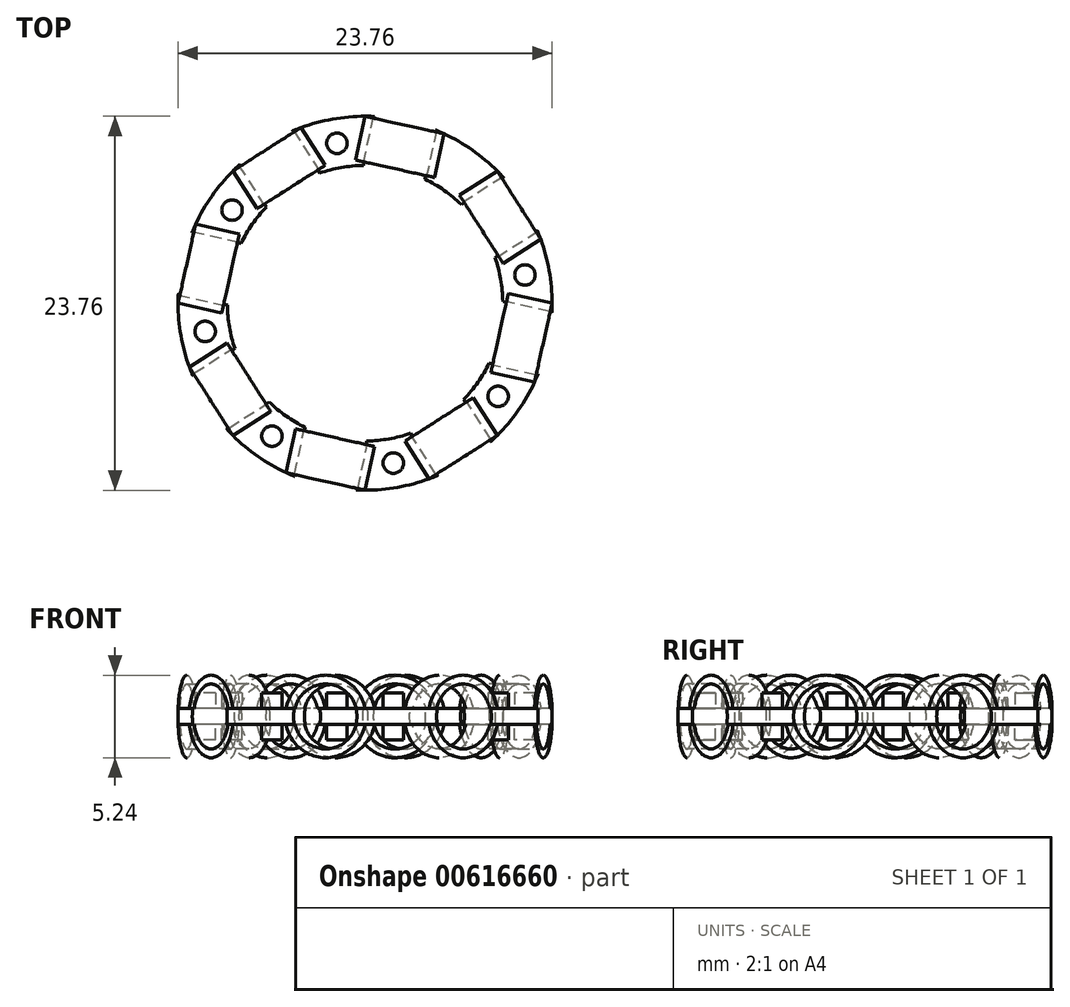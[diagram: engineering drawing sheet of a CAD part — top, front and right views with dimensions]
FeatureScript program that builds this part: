
annotation { "Feature Type Name" : "Feature", "Feature Type Description" : "" }
export const myFeature = defineFeature(function(context is Context, id is Id, definition is map)
    precondition{}
    {
        {
            var Q0;
            Q0=qCreatedBy(makeId("Top.planeOp"),FACE);
            var sketch = newSketch(context, id + "F0", { "sketchPlane" : qUnion([Q0])});
            skCircle(sketch, "E0", {"center": v(0, 0) * mm, "radius": 8.75 * mm});
            skCircle(sketch, "E1", {"center": v(0, 0) * mm, "radius": 11.88 * mm});
            skSolve(sketch);
        }
        {
            var Q0;
            Q0=makeQuery(id+"F0.imprint","IMPRINT",FACE,{"disambiguationData":[TD([[makeQuery(id+"F0.imprint","IMPRINT",EDGE,{"derivedFrom":sQuery(id+"F0.wireOp",EDGE,"E0")}),-1.0]])]});
            extrude(context, id + "F1", {"entities" : qUnion([Q0]), "endBound" : BoundingType.SYMMETRIC, "depth" : 1 * mm, "offsetDistance" : 25 * mm});
        }
        {
            var Q0;
            Q0=makeQuery(id+"F1.opExtrude","CAP_FACE",FACE,{"disambiguationData":[OSD([sQuery(id+"F0.wireOp",EDGE,"E0"),sQuery(id+"F0.wireOp",EDGE,"E1")])],"isStart":false});
            var sketch = newSketch(context, id + "F2", { "sketchPlane" : qUnion([Q0])});
            skPoint(sketch, "E2.center", {"position": v(0, 0) * mm});
            skLineSegment(sketch, "E3", {"start": v(0, 11.88) * mm, "end": v(1.04, 11.83) * mm});
            skLineSegment(sketch, "E4", {"start": v(1.04, 11.83) * mm, "end": v(2.06, 11.7) * mm});
            skLineSegment(sketch, "E5", {"start": v(2.06, 11.7) * mm, "end": v(3.07, 11.47) * mm});
            skLineSegment(sketch, "E6", {"start": v(3.07, 11.47) * mm, "end": v(4.06, 11.16) * mm});
            skLineSegment(sketch, "E7", {"start": v(4.06, 11.16) * mm, "end": v(5.02, 10.76) * mm});
            skLineSegment(sketch, "E8", {"start": v(5.02, 10.76) * mm, "end": v(5.94, 10.28) * mm});
            skLineSegment(sketch, "E9", {"start": v(5.94, 10.28) * mm, "end": v(6.81, 9.73) * mm});
            skLineSegment(sketch, "E10", {"start": v(6.81, 9.73) * mm, "end": v(7.63, 9.1) * mm});
            skLineSegment(sketch, "E11", {"start": v(7.63, 9.1) * mm, "end": v(8.4, 8.4) * mm});
            skLineSegment(sketch, "E12", {"start": v(4.37, 7.58) * mm, "end": v(5.02, 7.17) * mm});
            skLineSegment(sketch, "E13", {"start": v(5.02, 7.17) * mm, "end": v(5.62, 6.7) * mm});
            skLineSegment(sketch, "E14", {"start": v(5.62, 6.7) * mm, "end": v(6.19, 6.19) * mm});
            skCircle(sketch, "E15", {"center": v(5.91, 8.45) * mm, "radius": 0.65 * mm});
            skLineSegment(sketch, "E16.1.0", {"start": v(6, 6.87) * mm, "end": v(8.4, 8.4) * mm});
            skLineSegment(sketch, "E16.1.1", {"start": v(8.4, 8.4) * mm, "end": v(11.16, 4.06) * mm});
            skLineSegment(sketch, "E16.1.2", {"start": v(8.76, 2.53) * mm, "end": v(11.16, 4.06) * mm});
            skLineSegment(sketch, "E16.1.3", {"start": v(6, 6.87) * mm, "end": v(8.76, 2.53) * mm});
            skCircle(sketch, "E16.1.4", {"center": v(10.16, 1.8) * mm, "radius": 0.65 * mm});
            skLineSegment(sketch, "E16.2.0", {"start": v(9.1, 0.62) * mm, "end": v(11.88, 0) * mm});
            skLineSegment(sketch, "E16.2.1", {"start": v(11.88, 0) * mm, "end": v(10.76, -5.02) * mm});
            skLineSegment(sketch, "E16.2.2", {"start": v(7.99, -4.4) * mm, "end": v(10.76, -5.02) * mm});
            skLineSegment(sketch, "E16.2.3", {"start": v(9.1, 0.62) * mm, "end": v(7.99, -4.4) * mm});
            skCircle(sketch, "E16.2.4", {"center": v(8.45, -5.91) * mm, "radius": 0.65 * mm});
            skCircle(sketch, "E17.1.0", {"center": v(1.8, -10.16) * mm, "radius": 0.65 * mm});
            skLineSegment(sketch, "E17.1.1", {"start": v(6.87, -6) * mm, "end": v(2.53, -8.76) * mm});
            skLineSegment(sketch, "E17.1.2", {"start": v(6.87, -6) * mm, "end": v(8.4, -8.4) * mm});
            skLineSegment(sketch, "E17.1.3", {"start": v(8.4, -8.4) * mm, "end": v(4.06, -11.16) * mm});
            skLineSegment(sketch, "E17.1.4", {"start": v(2.53, -8.76) * mm, "end": v(4.06, -11.16) * mm});
            skCircle(sketch, "E17.2.0", {"center": v(-5.91, -8.45) * mm, "radius": 0.65 * mm});
            skLineSegment(sketch, "E17.2.1", {"start": v(0.62, -9.1) * mm, "end": v(-4.4, -7.99) * mm});
            skLineSegment(sketch, "E17.2.2", {"start": v(0.62, -9.1) * mm, "end": v(0, -11.88) * mm});
            skLineSegment(sketch, "E17.2.3", {"start": v(0, -11.88) * mm, "end": v(-5.02, -10.76) * mm});
            skLineSegment(sketch, "E17.2.4", {"start": v(-4.4, -7.99) * mm, "end": v(-5.02, -10.76) * mm});
            skCircle(sketch, "E18.1.0", {"center": v(-10.16, -1.8) * mm, "radius": 0.65 * mm});
            skLineSegment(sketch, "E18.1.1", {"start": v(-8.76, -2.53) * mm, "end": v(-11.16, -4.06) * mm});
            skLineSegment(sketch, "E18.1.2", {"start": v(-6, -6.87) * mm, "end": v(-8.76, -2.53) * mm});
            skLineSegment(sketch, "E18.1.3", {"start": v(-6, -6.87) * mm, "end": v(-8.4, -8.4) * mm});
            skLineSegment(sketch, "E18.1.4", {"start": v(-8.4, -8.4) * mm, "end": v(-11.16, -4.06) * mm});
            skCircle(sketch, "E18.2.0", {"center": v(-8.45, 5.91) * mm, "radius": 0.65 * mm});
            skLineSegment(sketch, "E18.2.1", {"start": v(-7.99, 4.4) * mm, "end": v(-10.76, 5.02) * mm});
            skLineSegment(sketch, "E18.2.2", {"start": v(-9.1, -0.62) * mm, "end": v(-7.99, 4.4) * mm});
            skLineSegment(sketch, "E18.2.3", {"start": v(-9.1, -0.62) * mm, "end": v(-11.88, 0) * mm});
            skLineSegment(sketch, "E18.2.4", {"start": v(-11.88, 0) * mm, "end": v(-10.76, 5.02) * mm});
            skLineSegment(sketch, "E19.1.0", {"start": v(-2.53, 8.76) * mm, "end": v(-4.06, 11.16) * mm});
            skLineSegment(sketch, "E19.1.1", {"start": v(-6.87, 6) * mm, "end": v(-2.53, 8.76) * mm});
            skLineSegment(sketch, "E19.1.2", {"start": v(-6.87, 6) * mm, "end": v(-8.4, 8.4) * mm});
            skLineSegment(sketch, "E19.1.3", {"start": v(-8.4, 8.4) * mm, "end": v(-4.06, 11.16) * mm});
            skCircle(sketch, "E19.1.4", {"center": v(-1.8, 10.16) * mm, "radius": 0.65 * mm});
            skLineSegment(sketch, "E19.2.0", {"start": v(4.4, 7.99) * mm, "end": v(5.02, 10.76) * mm});
            skLineSegment(sketch, "E19.2.2", {"start": v(-0.62, 9.1) * mm, "end": v(0, 11.88) * mm});
            skLineSegment(sketch, "E19.2.3", {"start": v(0, 11.88) * mm, "end": v(5.02, 10.76) * mm});
            skLineSegment(sketch, "E20", {"start": v(-0.62, 9.1) * mm, "end": v(4.4, 7.99) * mm});
            skSolve(sketch);
        }
        {
            var Q0;
            {var subQ2=sQuery(id+"F2.wireOp",EDGE,"E19.2.0");Q0=makeQuery(id+"F2.imprint","IMPRINT",FACE,{"disambiguationData":[TD([[makeQuery(id+"F2.imprint","IMPRINT",EDGE,{"derivedFrom":subQ2}),1.0]])]});}
            var Q1;
            {var subQ4=sQuery(id+"F2.wireOp",EDGE,"E16.1.0");Q1=makeQuery(id+"F2.imprint","IMPRINT",FACE,{"disambiguationData":[TD([[makeQuery(id+"F2.imprint","IMPRINT",EDGE,{"derivedFrom":subQ4}),-1.0]])]});}
            var Q2;
            {var subQ1=sQuery(id+"F2.wireOp",EDGE,"E16.2.0");Q2=makeQuery(id+"F2.imprint","IMPRINT",FACE,{"disambiguationData":[TD([[makeQuery(id+"F2.imprint","IMPRINT",EDGE,{"derivedFrom":subQ1}),-1.0]])]});}
            var Q3;
            {var subQ0=sQuery(id+"F2.wireOp",EDGE,"E17.1.2");Q3=makeQuery(id+"F2.imprint","IMPRINT",FACE,{"disambiguationData":[TD([[makeQuery(id+"F2.imprint","IMPRINT",EDGE,{"derivedFrom":subQ0}),-1.0]])]});}
            var Q4;
            {var subQ0=sQuery(id+"F2.wireOp",EDGE,"E17.2.2");Q4=makeQuery(id+"F2.imprint","IMPRINT",FACE,{"disambiguationData":[TD([[makeQuery(id+"F2.imprint","IMPRINT",EDGE,{"derivedFrom":subQ0}),-1.0]])]});}
            var Q5;
            {var subQ2=sQuery(id+"F2.wireOp",EDGE,"E18.1.1");Q5=makeQuery(id+"F2.imprint","IMPRINT",FACE,{"disambiguationData":[TD([[makeQuery(id+"F2.imprint","IMPRINT",EDGE,{"derivedFrom":subQ2}),1.0]])]});}
            var Q6;
            {var subQ2=sQuery(id+"F2.wireOp",EDGE,"E19.1.0");Q6=makeQuery(id+"F2.imprint","IMPRINT",FACE,{"disambiguationData":[TD([[makeQuery(id+"F2.imprint","IMPRINT",EDGE,{"derivedFrom":subQ2}),1.0]])]});}
            var Q7;
            {var subQ2=sQuery(id+"F2.wireOp",EDGE,"E18.2.1");Q7=makeQuery(id+"F2.imprint","IMPRINT",FACE,{"disambiguationData":[TD([[makeQuery(id+"F2.imprint","IMPRINT",EDGE,{"derivedFrom":subQ2}),1.0]])]});}
            extrude(context, id + "F3", {"entities" : qUnion([Q0, Q1, Q2, Q3, Q4, Q5, Q6, Q7]), "operationType" : NewBodyOperationType.ADD, "depth" : 2.12 * mm, "offsetDistance" : 25 * mm});
        }
        {
            var Q0;
            Q0=makeQuery(id+"F3.opExtrude","CAP_FACE",FACE,{"disambiguationData":[OSD([sQuery(id+"F2.wireOp",EDGE,"E19.2.0"),sQuery(id+"F2.wireOp",EDGE,"E19.2.2"),sQuery(id+"F2.wireOp",EDGE,"E19.2.3"),sQuery(id+"F2.wireOp",EDGE,"E20")])],"isStart":false});
            var Q1;
            Q1=makeQuery(id+"F3.opExtrude","CAP_FACE",FACE,{"disambiguationData":[OSD([sQuery(id+"F2.wireOp",EDGE,"E19.1.0"),sQuery(id+"F2.wireOp",EDGE,"E19.1.1"),sQuery(id+"F2.wireOp",EDGE,"E19.1.2"),sQuery(id+"F2.wireOp",EDGE,"E19.1.3")])],"isStart":false});
            var Q2;
            Q2=makeQuery(id+"F3.opExtrude","CAP_FACE",FACE,{"disambiguationData":[OSD([sQuery(id+"F2.wireOp",EDGE,"E18.2.1"),sQuery(id+"F2.wireOp",EDGE,"E18.2.2"),sQuery(id+"F2.wireOp",EDGE,"E18.2.3"),sQuery(id+"F2.wireOp",EDGE,"E18.2.4")])],"isStart":false});
            var Q3;
            Q3=makeQuery(id+"F3.opExtrude","CAP_FACE",FACE,{"disambiguationData":[OSD([sQuery(id+"F2.wireOp",EDGE,"E18.1.1"),sQuery(id+"F2.wireOp",EDGE,"E18.1.2"),sQuery(id+"F2.wireOp",EDGE,"E18.1.3"),sQuery(id+"F2.wireOp",EDGE,"E18.1.4")])],"isStart":false});
            var Q4;
            Q4=makeQuery(id+"F3.opExtrude","CAP_FACE",FACE,{"disambiguationData":[OSD([sQuery(id+"F2.wireOp",EDGE,"E17.2.1"),sQuery(id+"F2.wireOp",EDGE,"E17.2.2"),sQuery(id+"F2.wireOp",EDGE,"E17.2.3"),sQuery(id+"F2.wireOp",EDGE,"E17.2.4")])],"isStart":false});
            var Q5;
            Q5=makeQuery(id+"F3.opExtrude","CAP_FACE",FACE,{"disambiguationData":[OSD([sQuery(id+"F2.wireOp",EDGE,"E17.1.1"),sQuery(id+"F2.wireOp",EDGE,"E17.1.2"),sQuery(id+"F2.wireOp",EDGE,"E17.1.3"),sQuery(id+"F2.wireOp",EDGE,"E17.1.4")])],"isStart":false});
            var Q6;
            Q6=makeQuery(id+"F3.opExtrude","CAP_FACE",FACE,{"disambiguationData":[OSD([sQuery(id+"F2.wireOp",EDGE,"E16.2.0"),sQuery(id+"F2.wireOp",EDGE,"E16.2.1"),sQuery(id+"F2.wireOp",EDGE,"E16.2.2"),sQuery(id+"F2.wireOp",EDGE,"E16.2.3")])],"isStart":false});
            var Q7;
            Q7=makeQuery(id+"F3.opExtrude","CAP_FACE",FACE,{"disambiguationData":[OSD([sQuery(id+"F2.wireOp",EDGE,"E16.1.0"),sQuery(id+"F2.wireOp",EDGE,"E16.1.1"),sQuery(id+"F2.wireOp",EDGE,"E16.1.2"),sQuery(id+"F2.wireOp",EDGE,"E16.1.3")])],"isStart":false});
            extrude(context, id + "F4", {"entities" : qUnion([Q0, Q1, Q2, Q3, Q4, Q5, Q6, Q7]), "operationType" : NewBodyOperationType.ADD, "oppositeDirection" : true, "depth" : 5.25 * mm, "offsetDistance" : 25 * mm});
        }
        {
            var Q0;
            Q0=makeQuery(id+"F2.imprint","IMPRINT",FACE,{"disambiguationData":[TD([[makeQuery(id+"F2.imprint","IMPRINT",EDGE,{"derivedFrom":sQuery(id+"F2.wireOp",EDGE,"E17.2.0")}),1.0]])]});
            var Q1;
            Q1=makeQuery(id+"F2.imprint","IMPRINT",FACE,{"disambiguationData":[TD([[makeQuery(id+"F2.imprint","IMPRINT",EDGE,{"derivedFrom":sQuery(id+"F2.wireOp",EDGE,"E18.1.0")}),1.0]])]});
            var Q2;
            Q2=makeQuery(id+"F2.imprint","IMPRINT",FACE,{"disambiguationData":[TD([[makeQuery(id+"F2.imprint","IMPRINT",EDGE,{"derivedFrom":sQuery(id+"F2.wireOp",EDGE,"E18.2.0")}),1.0]])]});
            var Q3;
            Q3=makeQuery(id+"F2.imprint","IMPRINT",FACE,{"disambiguationData":[TD([[makeQuery(id+"F2.imprint","IMPRINT",EDGE,{"derivedFrom":sQuery(id+"F2.wireOp",EDGE,"E19.1.4")}),1.0]])]});
            var Q4;
            Q4=makeQuery(id+"F2.imprint","IMPRINT",FACE,{"disambiguationData":[TD([[makeQuery(id+"F2.imprint","IMPRINT",EDGE,{"derivedFrom":sQuery(id+"F2.wireOp",EDGE,"E15")}),1.0]])]});
            var Q5;
            Q5=makeQuery(id+"F2.imprint","IMPRINT",FACE,{"disambiguationData":[TD([[makeQuery(id+"F2.imprint","IMPRINT",EDGE,{"derivedFrom":sQuery(id+"F2.wireOp",EDGE,"E16.1.4")}),1.0]])]});
            var Q6;
            Q6=makeQuery(id+"F2.imprint","IMPRINT",FACE,{"disambiguationData":[TD([[makeQuery(id+"F2.imprint","IMPRINT",EDGE,{"derivedFrom":sQuery(id+"F2.wireOp",EDGE,"E17.1.0")}),1.0]])]});
            var Q7;
            Q7=makeQuery(id+"F2.imprint","IMPRINT",FACE,{"disambiguationData":[TD([[makeQuery(id+"F2.imprint","IMPRINT",EDGE,{"derivedFrom":sQuery(id+"F2.wireOp",EDGE,"E16.2.4")}),1.0]])]});
            extrude(context, id + "F5", {"entities" : qUnion([Q0, Q1, Q2, Q3, Q4, Q5, Q6, Q7]), "operationType" : NewBodyOperationType.ADD, "depth" : 1 * mm, "offsetDistance" : 25 * mm});
        }
        {
            var Q0;
            Q0=makeQuery(id+"F2.imprint","IMPRINT",FACE,{"disambiguationData":[TD([[makeQuery(id+"F2.imprint","IMPRINT",EDGE,{"derivedFrom":sQuery(id+"F2.wireOp",EDGE,"E15")}),1.0]])]});
            var Q1;
            Q1=makeQuery(id+"F2.imprint","IMPRINT",FACE,{"disambiguationData":[TD([[makeQuery(id+"F2.imprint","IMPRINT",EDGE,{"derivedFrom":sQuery(id+"F2.wireOp",EDGE,"E19.1.4")}),1.0]])]});
            var Q2;
            Q2=makeQuery(id+"F2.imprint","IMPRINT",FACE,{"disambiguationData":[TD([[makeQuery(id+"F2.imprint","IMPRINT",EDGE,{"derivedFrom":sQuery(id+"F2.wireOp",EDGE,"E18.2.0")}),1.0]])]});
            var Q3;
            Q3=makeQuery(id+"F2.imprint","IMPRINT",FACE,{"disambiguationData":[TD([[makeQuery(id+"F2.imprint","IMPRINT",EDGE,{"derivedFrom":sQuery(id+"F2.wireOp",EDGE,"E16.1.4")}),1.0]])]});
            var Q4;
            Q4=makeQuery(id+"F2.imprint","IMPRINT",FACE,{"disambiguationData":[TD([[makeQuery(id+"F2.imprint","IMPRINT",EDGE,{"derivedFrom":sQuery(id+"F2.wireOp",EDGE,"E16.2.4")}),1.0]])]});
            var Q5;
            Q5=makeQuery(id+"F2.imprint","IMPRINT",FACE,{"disambiguationData":[TD([[makeQuery(id+"F2.imprint","IMPRINT",EDGE,{"derivedFrom":sQuery(id+"F2.wireOp",EDGE,"E17.1.0")}),1.0]])]});
            var Q6;
            Q6=makeQuery(id+"F2.imprint","IMPRINT",FACE,{"disambiguationData":[TD([[makeQuery(id+"F2.imprint","IMPRINT",EDGE,{"derivedFrom":sQuery(id+"F2.wireOp",EDGE,"E17.2.0")}),1.0]])]});
            var Q7;
            Q7=makeQuery(id+"F2.imprint","IMPRINT",FACE,{"disambiguationData":[TD([[makeQuery(id+"F2.imprint","IMPRINT",EDGE,{"derivedFrom":sQuery(id+"F2.wireOp",EDGE,"E18.1.0")}),1.0]])]});
            extrude(context, id + "F6", {"entities" : qUnion([Q0, Q1, Q2, Q3, Q4, Q5, Q6, Q7]), "operationType" : NewBodyOperationType.ADD, "oppositeDirection" : true, "depth" : 2 * mm, "offsetDistance" : 25 * mm});
        }
        {
            var Q0;
            Q0=makeQuery(id+"F3.opExtrude","CAP_EDGE",EDGE,{"disambiguationData":[OSD([sQuery(id+"F2.wireOp",EDGE,"E19.2.0")])],"isStart":false});
            var Q1;
            Q1=makeQuery(id+"F3.opExtrude","CAP_EDGE",EDGE,{"disambiguationData":[OSD([sQuery(id+"F2.wireOp",EDGE,"E19.1.0")])],"isStart":false});
            var Q2;
            Q2=makeQuery(id+"F3.opExtrude","CAP_EDGE",EDGE,{"disambiguationData":[OSD([sQuery(id+"F2.wireOp",EDGE,"E18.2.1")])],"isStart":false});
            var Q3;
            Q3=makeQuery(id+"F3.opExtrude","CAP_EDGE",EDGE,{"disambiguationData":[OSD([sQuery(id+"F2.wireOp",EDGE,"E18.1.1")])],"isStart":false});
            var Q4;
            Q4=makeQuery(id+"F3.opExtrude","CAP_EDGE",EDGE,{"disambiguationData":[OSD([sQuery(id+"F2.wireOp",EDGE,"E18.1.3")])],"isStart":false});
            var Q5;
            Q5=makeQuery(id+"F3.opExtrude","CAP_EDGE",EDGE,{"disambiguationData":[OSD([sQuery(id+"F2.wireOp",EDGE,"E17.2.4")])],"isStart":false});
            var Q6;
            Q6=makeQuery(id+"F3.opExtrude","CAP_EDGE",EDGE,{"disambiguationData":[OSD([sQuery(id+"F2.wireOp",EDGE,"E17.2.2")])],"isStart":false});
            var Q7;
            Q7=makeQuery(id+"F3.opExtrude","CAP_EDGE",EDGE,{"disambiguationData":[OSD([sQuery(id+"F2.wireOp",EDGE,"E17.1.4")])],"isStart":false});
            var Q8;
            Q8=makeQuery(id+"F3.opExtrude","CAP_EDGE",EDGE,{"disambiguationData":[OSD([sQuery(id+"F2.wireOp",EDGE,"E17.1.2")])],"isStart":false});
            var Q9;
            Q9=makeQuery(id+"F3.opExtrude","CAP_EDGE",EDGE,{"disambiguationData":[OSD([sQuery(id+"F2.wireOp",EDGE,"E16.2.2")])],"isStart":false});
            var Q10;
            Q10=makeQuery(id+"F3.opExtrude","CAP_EDGE",EDGE,{"disambiguationData":[OSD([sQuery(id+"F2.wireOp",EDGE,"E16.2.0")])],"isStart":false});
            var Q11;
            Q11=makeQuery(id+"F3.opExtrude","CAP_EDGE",EDGE,{"disambiguationData":[OSD([sQuery(id+"F2.wireOp",EDGE,"E16.1.2")])],"isStart":false});
            var Q12;
            Q12=makeQuery(id+"F3.opExtrude","CAP_EDGE",EDGE,{"disambiguationData":[OSD([sQuery(id+"F2.wireOp",EDGE,"E16.1.0")])],"isStart":false});
            var Q13;
            Q13=makeQuery(id+"F3.opExtrude","CAP_EDGE",EDGE,{"disambiguationData":[OSD([sQuery(id+"F2.wireOp",EDGE,"E18.2.3")])],"isStart":false});
            var Q14;
            Q14=makeQuery(id+"F3.opExtrude","CAP_EDGE",EDGE,{"disambiguationData":[OSD([sQuery(id+"F2.wireOp",EDGE,"E19.1.2")])],"isStart":false});
            var Q15;
            Q15=makeQuery(id+"F3.opExtrude","CAP_EDGE",EDGE,{"disambiguationData":[OSD([sQuery(id+"F2.wireOp",EDGE,"E19.2.2")])],"isStart":false});
            fillet(context, id + "F7", {"entities" : qUnion([Q0, Q1, Q2, Q3, Q4, Q5, Q6, Q7, Q8, Q9, Q10, Q11, Q12, Q13, Q14, Q15]), "radius" : 2.62 * mm, "tangentPropagation" : true, "allowEdgeOverflow" : false});
        }
        {
            var Q0;
            Q0=makeQuery(id+"F4.opExtrude","CAP_EDGE",EDGE,{"disambiguationData":[OSD([sQuery(id+"F2.wireOp",EDGE,"E17.2.2")])],"isStart":false});
            var Q1;
            Q1=makeQuery(id+"F4.opExtrude","CAP_EDGE",EDGE,{"disambiguationData":[OSD([sQuery(id+"F2.wireOp",EDGE,"E17.2.4")])],"isStart":false});
            var Q2;
            Q2=makeQuery(id+"F4.opExtrude","CAP_EDGE",EDGE,{"disambiguationData":[OSD([sQuery(id+"F2.wireOp",EDGE,"E18.1.3")])],"isStart":false});
            var Q3;
            Q3=makeQuery(id+"F4.opExtrude","CAP_EDGE",EDGE,{"disambiguationData":[OSD([sQuery(id+"F2.wireOp",EDGE,"E18.1.1")])],"isStart":false});
            var Q4;
            Q4=makeQuery(id+"F4.opExtrude","CAP_EDGE",EDGE,{"disambiguationData":[OSD([sQuery(id+"F2.wireOp",EDGE,"E18.2.3")])],"isStart":false});
            var Q5;
            Q5=makeQuery(id+"F4.opExtrude","CAP_EDGE",EDGE,{"disambiguationData":[OSD([sQuery(id+"F2.wireOp",EDGE,"E18.2.1")])],"isStart":false});
            var Q6;
            Q6=makeQuery(id+"F4.opExtrude","CAP_EDGE",EDGE,{"disambiguationData":[OSD([sQuery(id+"F2.wireOp",EDGE,"E19.1.2")])],"isStart":false});
            var Q7;
            Q7=makeQuery(id+"F4.opExtrude","CAP_EDGE",EDGE,{"disambiguationData":[OSD([sQuery(id+"F2.wireOp",EDGE,"E19.1.0")])],"isStart":false});
            var Q8;
            Q8=makeQuery(id+"F4.opExtrude","CAP_EDGE",EDGE,{"disambiguationData":[OSD([sQuery(id+"F2.wireOp",EDGE,"E19.2.2")])],"isStart":false});
            var Q9;
            Q9=makeQuery(id+"F4.opExtrude","CAP_EDGE",EDGE,{"disambiguationData":[OSD([sQuery(id+"F2.wireOp",EDGE,"E19.2.0")])],"isStart":false});
            var Q10;
            Q10=makeQuery(id+"F4.opExtrude","CAP_EDGE",EDGE,{"disambiguationData":[OSD([sQuery(id+"F2.wireOp",EDGE,"E16.1.0")])],"isStart":false});
            var Q11;
            Q11=makeQuery(id+"F4.opExtrude","CAP_EDGE",EDGE,{"disambiguationData":[OSD([sQuery(id+"F2.wireOp",EDGE,"E16.1.2")])],"isStart":false});
            var Q12;
            Q12=makeQuery(id+"F4.opExtrude","CAP_EDGE",EDGE,{"disambiguationData":[OSD([sQuery(id+"F2.wireOp",EDGE,"E16.2.0")])],"isStart":false});
            var Q13;
            Q13=makeQuery(id+"F4.opExtrude","CAP_EDGE",EDGE,{"disambiguationData":[OSD([sQuery(id+"F2.wireOp",EDGE,"E16.2.2")])],"isStart":false});
            var Q14;
            Q14=makeQuery(id+"F4.opExtrude","CAP_EDGE",EDGE,{"disambiguationData":[OSD([sQuery(id+"F2.wireOp",EDGE,"E17.1.2")])],"isStart":false});
            var Q15;
            Q15=makeQuery(id+"F4.opExtrude","CAP_EDGE",EDGE,{"disambiguationData":[OSD([sQuery(id+"F2.wireOp",EDGE,"E17.1.4")])],"isStart":false});
            fillet(context, id + "F8", {"entities" : qUnion([Q0, Q1, Q2, Q3, Q4, Q5, Q6, Q7, Q8, Q9, Q10, Q11, Q12, Q13, Q14, Q15]), "radius" : 2.62 * mm, "tangentPropagation" : true, "allowEdgeOverflow" : false});
        }
        {
            var Q0;
            Q0=makeQuery(id+"F3.opExtrude","SWEPT_FACE",FACE,{"disambiguationData":[OSD([sQuery(id+"F2.wireOp",EDGE,"E19.1.1")])]});
            var sketch = newSketch(context, id + "F9", { "sketchPlane" : qUnion([Q0])});
            skCircle(sketch, "E21", {"center": v(0, 0) * mm, "radius": 2.06 * mm});
            skSolve(sketch);
        }
        {
            var Q0;
            Q0=makeQuery(id+"F3.opExtrude","SWEPT_FACE",FACE,{"disambiguationData":[OSD([sQuery(id+"F2.wireOp",EDGE,"E20")])]});
            var sketch = newSketch(context, id + "F10", { "sketchPlane" : qUnion([Q0])});
            skCircle(sketch, "E22", {"center": v(0, 0) * mm, "radius": 2.06 * mm});
            skSolve(sketch);
        }
        {
            var Q0;
            Q0=makeQuery(id+"F3.opExtrude","SWEPT_FACE",FACE,{"disambiguationData":[OSD([sQuery(id+"F2.wireOp",EDGE,"E16.1.3")])]});
            var sketch = newSketch(context, id + "F11", { "sketchPlane" : qUnion([Q0])});
            skCircle(sketch, "E23", {"center": v(0, 0) * mm, "radius": 2.06 * mm});
            skSolve(sketch);
        }
        {
            var Q0;
            Q0=makeQuery(id+"F3.opExtrude","SWEPT_FACE",FACE,{"disambiguationData":[OSD([sQuery(id+"F2.wireOp",EDGE,"E16.2.3")])]});
            var sketch = newSketch(context, id + "F12", { "sketchPlane" : qUnion([Q0])});
            skCircle(sketch, "E24", {"center": v(0, 0) * mm, "radius": 2.06 * mm});
            skSolve(sketch);
        }
        {
            var Q0;
            {var subQ0=sQuery(id+"F9.wireOp",EDGE,"E21");var subQ4=sQuery(id+"F2.wireOp",EDGE,"E19.1.1");var subQ6=makeQuery(id+"F3.opExtrude","CAP_EDGE",EDGE,{"disambiguationData":[OSD([subQ4])],"isStart":true});var subQ7=makeQuery(id+"F3.boolean.opBoolean","SPLIT",EDGE,{"disambiguationData":[TD([makeQuery(id+"F3.opExtrude","SWEPT_FACE",FACE,{"disambiguationData":[OSD([sQuery(id+"F2.wireOp",EDGE,"E19.1.0")])]})])],"derivedFrom":subQ6});var subQ8=makeQuery(id+"F9.imprint","INTERSECT",VERTEX,{"derivedFrom":[subQ7,subQ0]});Q0=makeQuery(id+"F9.imprint","IMPRINT",FACE,{"disambiguationData":[TD([[makeQuery(id+"F9.imprint","IMPRINT",EDGE,{"disambiguationData":[TD([[subQ8,-1.0]])],"derivedFrom":subQ0}),1.0]])]});}
            var Q1;
            {var subQ0=sQuery(id+"F9.wireOp",EDGE,"E21");var subQ4=sQuery(id+"F2.wireOp",EDGE,"E19.1.1");var subQ6=makeQuery(id+"F3.opExtrude","CAP_EDGE",EDGE,{"disambiguationData":[OSD([subQ4])],"isStart":true});var subQ7=makeQuery(id+"F3.boolean.opBoolean","SPLIT",EDGE,{"disambiguationData":[TD([makeQuery(id+"F3.opExtrude","SWEPT_FACE",FACE,{"disambiguationData":[OSD([sQuery(id+"F2.wireOp",EDGE,"E19.1.0")])]})])],"derivedFrom":subQ6});var subQ8=makeQuery(id+"F9.imprint","INTERSECT",VERTEX,{"derivedFrom":[subQ7,subQ0]});Q1=makeQuery(id+"F9.imprint","IMPRINT",FACE,{"disambiguationData":[TD([[makeQuery(id+"F9.imprint","IMPRINT",EDGE,{"disambiguationData":[TD([[subQ8,1.0]])],"derivedFrom":subQ0}),1.0]])]});}
            var Q2;
            Q2=sQuery(id+"F9.wireOp",EDGE,"Q23HQU0p-Jsze-Z4cs-K9uM-0FIPc1pSfwWw");
            extrude(context, id + "F13", {"entities" : qUnion([Q0, Q1]), "operationType" : NewBodyOperationType.REMOVE, "surfaceEntities" : qUnion([Q2]), "endBound" : BoundingType.SYMMETRIC, "oppositeDirection" : true, "depth" : 55 * mm, "offsetDistance" : 25 * mm});
        }
        {
            var Q0;
            {var subQ0=sQuery(id+"F10.wireOp",EDGE,"E22");var subQ3=sQuery(id+"F2.wireOp",EDGE,"E20");var subQ6=makeQuery(id+"F3.opExtrude","CAP_EDGE",EDGE,{"disambiguationData":[OSD([subQ3])],"isStart":true});var subQ7=makeQuery(id+"F3.boolean.opBoolean","SPLIT",EDGE,{"disambiguationData":[TD([makeQuery(id+"F3.opExtrude","SWEPT_FACE",FACE,{"disambiguationData":[OSD([sQuery(id+"F2.wireOp",EDGE,"E19.2.0")])]})])],"derivedFrom":subQ6});var subQ8=makeQuery(id+"F10.imprint","INTERSECT",VERTEX,{"derivedFrom":[subQ7,subQ0]});Q0=makeQuery(id+"F10.imprint","IMPRINT",FACE,{"disambiguationData":[TD([[makeQuery(id+"F10.imprint","IMPRINT",EDGE,{"disambiguationData":[TD([[subQ8,-1.0]])],"derivedFrom":subQ0}),1.0]])]});}
            var Q1;
            {var subQ0=sQuery(id+"F10.wireOp",EDGE,"E22");var subQ3=sQuery(id+"F2.wireOp",EDGE,"E20");var subQ6=makeQuery(id+"F3.opExtrude","CAP_EDGE",EDGE,{"disambiguationData":[OSD([subQ3])],"isStart":true});var subQ7=makeQuery(id+"F3.boolean.opBoolean","SPLIT",EDGE,{"disambiguationData":[TD([makeQuery(id+"F3.opExtrude","SWEPT_FACE",FACE,{"disambiguationData":[OSD([sQuery(id+"F2.wireOp",EDGE,"E19.2.0")])]})])],"derivedFrom":subQ6});var subQ8=makeQuery(id+"F10.imprint","INTERSECT",VERTEX,{"derivedFrom":[subQ7,subQ0]});Q1=makeQuery(id+"F10.imprint","IMPRINT",FACE,{"disambiguationData":[TD([[makeQuery(id+"F10.imprint","IMPRINT",EDGE,{"disambiguationData":[TD([[subQ8,1.0]])],"derivedFrom":subQ0}),1.0]])]});}
            extrude(context, id + "F14", {"entities" : qUnion([Q0, Q1]), "operationType" : NewBodyOperationType.REMOVE, "endBound" : BoundingType.SYMMETRIC, "oppositeDirection" : true, "depth" : 55 * mm, "offsetDistance" : 25 * mm});
        }
        {
            var Q0;
            {var subQ0=sQuery(id+"F11.wireOp",EDGE,"E23");var subQ4=sQuery(id+"F2.wireOp",EDGE,"E16.1.3");var subQ6=makeQuery(id+"F3.opExtrude","CAP_EDGE",EDGE,{"disambiguationData":[OSD([subQ4])],"isStart":true});var subQ7=makeQuery(id+"F3.boolean.opBoolean","SPLIT",EDGE,{"disambiguationData":[TD([makeQuery(id+"F3.opExtrude","SWEPT_FACE",FACE,{"disambiguationData":[OSD([sQuery(id+"F2.wireOp",EDGE,"E16.1.0")])]})])],"derivedFrom":subQ6});var subQ8=makeQuery(id+"F11.imprint","INTERSECT",VERTEX,{"derivedFrom":[subQ7,subQ0]});Q0=makeQuery(id+"F11.imprint","IMPRINT",FACE,{"disambiguationData":[TD([[makeQuery(id+"F11.imprint","IMPRINT",EDGE,{"disambiguationData":[TD([[subQ8,1.0]])],"derivedFrom":subQ0}),1.0]])]});}
            var Q1;
            {var subQ0=sQuery(id+"F11.wireOp",EDGE,"E23");var subQ4=sQuery(id+"F2.wireOp",EDGE,"E16.1.3");var subQ6=makeQuery(id+"F3.opExtrude","CAP_EDGE",EDGE,{"disambiguationData":[OSD([subQ4])],"isStart":true});var subQ7=makeQuery(id+"F3.boolean.opBoolean","SPLIT",EDGE,{"disambiguationData":[TD([makeQuery(id+"F3.opExtrude","SWEPT_FACE",FACE,{"disambiguationData":[OSD([sQuery(id+"F2.wireOp",EDGE,"E16.1.0")])]})])],"derivedFrom":subQ6});var subQ8=makeQuery(id+"F11.imprint","INTERSECT",VERTEX,{"derivedFrom":[subQ7,subQ0]});Q1=makeQuery(id+"F11.imprint","IMPRINT",FACE,{"disambiguationData":[TD([[makeQuery(id+"F11.imprint","IMPRINT",EDGE,{"disambiguationData":[TD([[subQ8,-1.0]])],"derivedFrom":subQ0}),1.0]])]});}
            extrude(context, id + "F15", {"entities" : qUnion([Q0, Q1]), "operationType" : NewBodyOperationType.REMOVE, "endBound" : BoundingType.SYMMETRIC, "oppositeDirection" : true, "depth" : 55 * mm, "offsetDistance" : 25 * mm});
        }
        {
            var Q0;
            {var subQ0=sQuery(id+"F12.wireOp",EDGE,"E24");var subQ4=sQuery(id+"F2.wireOp",EDGE,"E16.2.3");var subQ6=makeQuery(id+"F3.opExtrude","CAP_EDGE",EDGE,{"disambiguationData":[OSD([subQ4])],"isStart":true});var subQ7=makeQuery(id+"F3.boolean.opBoolean","SPLIT",EDGE,{"disambiguationData":[TD([makeQuery(id+"F3.opExtrude","SWEPT_FACE",FACE,{"disambiguationData":[OSD([sQuery(id+"F2.wireOp",EDGE,"E16.2.0")])]})])],"derivedFrom":subQ6});var subQ8=makeQuery(id+"F12.imprint","INTERSECT",VERTEX,{"derivedFrom":[subQ7,subQ0]});Q0=makeQuery(id+"F12.imprint","IMPRINT",FACE,{"disambiguationData":[TD([[makeQuery(id+"F12.imprint","IMPRINT",EDGE,{"disambiguationData":[TD([[subQ8,1.0]])],"derivedFrom":subQ0}),1.0]])]});}
            var Q1;
            {var subQ0=sQuery(id+"F12.wireOp",EDGE,"E24");var subQ4=sQuery(id+"F2.wireOp",EDGE,"E16.2.3");var subQ6=makeQuery(id+"F3.opExtrude","CAP_EDGE",EDGE,{"disambiguationData":[OSD([subQ4])],"isStart":true});var subQ7=makeQuery(id+"F3.boolean.opBoolean","SPLIT",EDGE,{"disambiguationData":[TD([makeQuery(id+"F3.opExtrude","SWEPT_FACE",FACE,{"disambiguationData":[OSD([sQuery(id+"F2.wireOp",EDGE,"E16.2.0")])]})])],"derivedFrom":subQ6});var subQ8=makeQuery(id+"F12.imprint","INTERSECT",VERTEX,{"derivedFrom":[subQ7,subQ0]});Q1=makeQuery(id+"F12.imprint","IMPRINT",FACE,{"disambiguationData":[TD([[makeQuery(id+"F12.imprint","IMPRINT",EDGE,{"disambiguationData":[TD([[subQ8,-1.0]])],"derivedFrom":subQ0}),1.0]])]});}
            extrude(context, id + "F16", {"entities" : qUnion([Q0, Q1]), "operationType" : NewBodyOperationType.REMOVE, "endBound" : BoundingType.SYMMETRIC, "depth" : 55 * mm, "offsetDistance" : 25 * mm});
        }
    });
